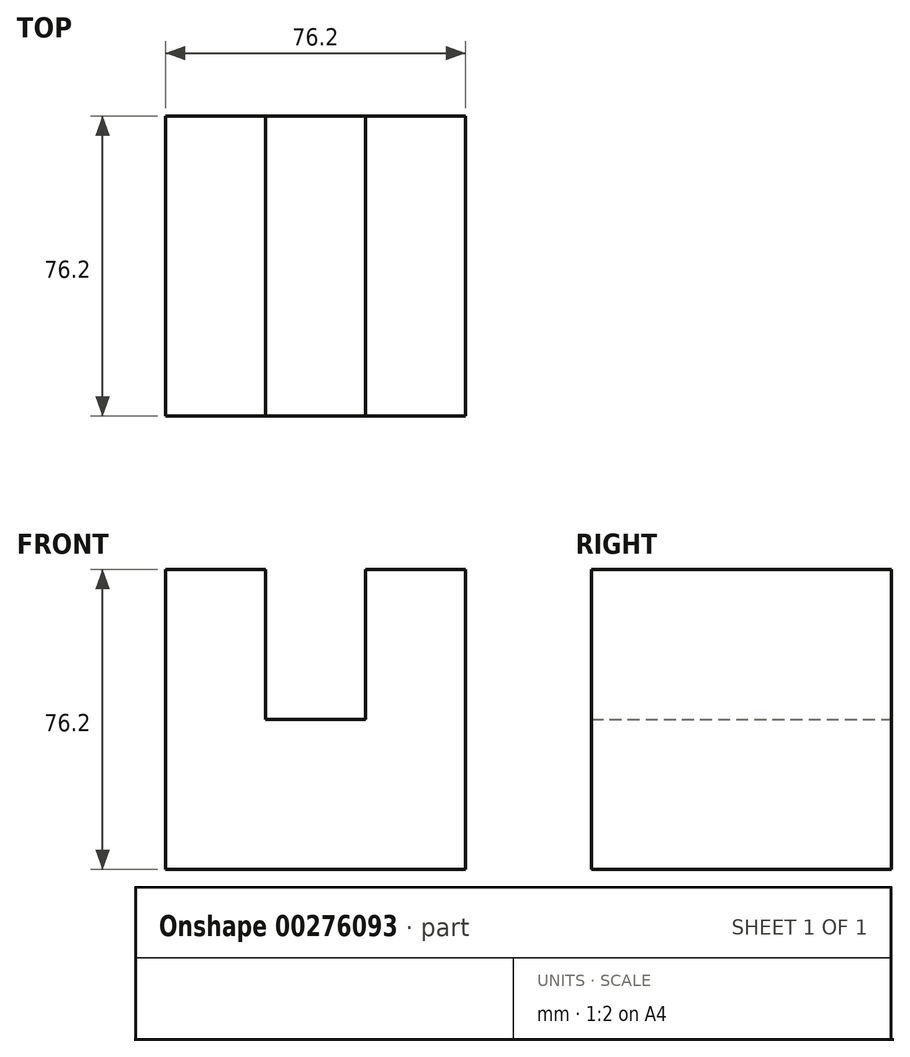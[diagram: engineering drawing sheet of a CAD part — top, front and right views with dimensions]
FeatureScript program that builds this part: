
annotation { "Feature Type Name" : "Feature", "Feature Type Description" : "" }
export const myFeature = defineFeature(function(context is Context, id is Id, definition is map)
    precondition{}
    {
        {
            var Q0;
            Q0=qCreatedBy(makeId("Front.planeOp"),FACE);
            var sketch = newSketch(context, id + "F0", { "sketchPlane" : qUnion([Q0])});
            skLineSegment(sketch, "E0", {"start": v(0, 0) * mm, "end": v(0, 76.2) * mm});
            skLineSegment(sketch, "E1", {"start": v(0, 76.2) * mm, "end": v(-25.4, 76.2) * mm});
            skLineSegment(sketch, "E2", {"start": v(-25.4, 76.2) * mm, "end": v(-25.4, 38.1) * mm});
            skLineSegment(sketch, "E3", {"start": v(-25.4, 38.1) * mm, "end": v(-50.8, 38.1) * mm});
            skLineSegment(sketch, "E4", {"start": v(-50.8, 38.1) * mm, "end": v(-50.8, 76.2) * mm});
            skLineSegment(sketch, "E5", {"start": v(-50.8, 76.2) * mm, "end": v(-76.2, 76.2) * mm});
            skLineSegment(sketch, "E6", {"start": v(-76.2, 76.2) * mm, "end": v(-76.2, 0) * mm});
            skLineSegment(sketch, "E7", {"start": v(-76.2, 0) * mm, "end": v(0, 0) * mm});
            skSolve(sketch);
        }
        {
            var Q0;
            Q0 = qSketchRegion(id + "F0", true);
            extrude(context, id + "F1", {"entities" : qUnion([Q0]), "depth" : 76.2 * mm});
        }
    });
